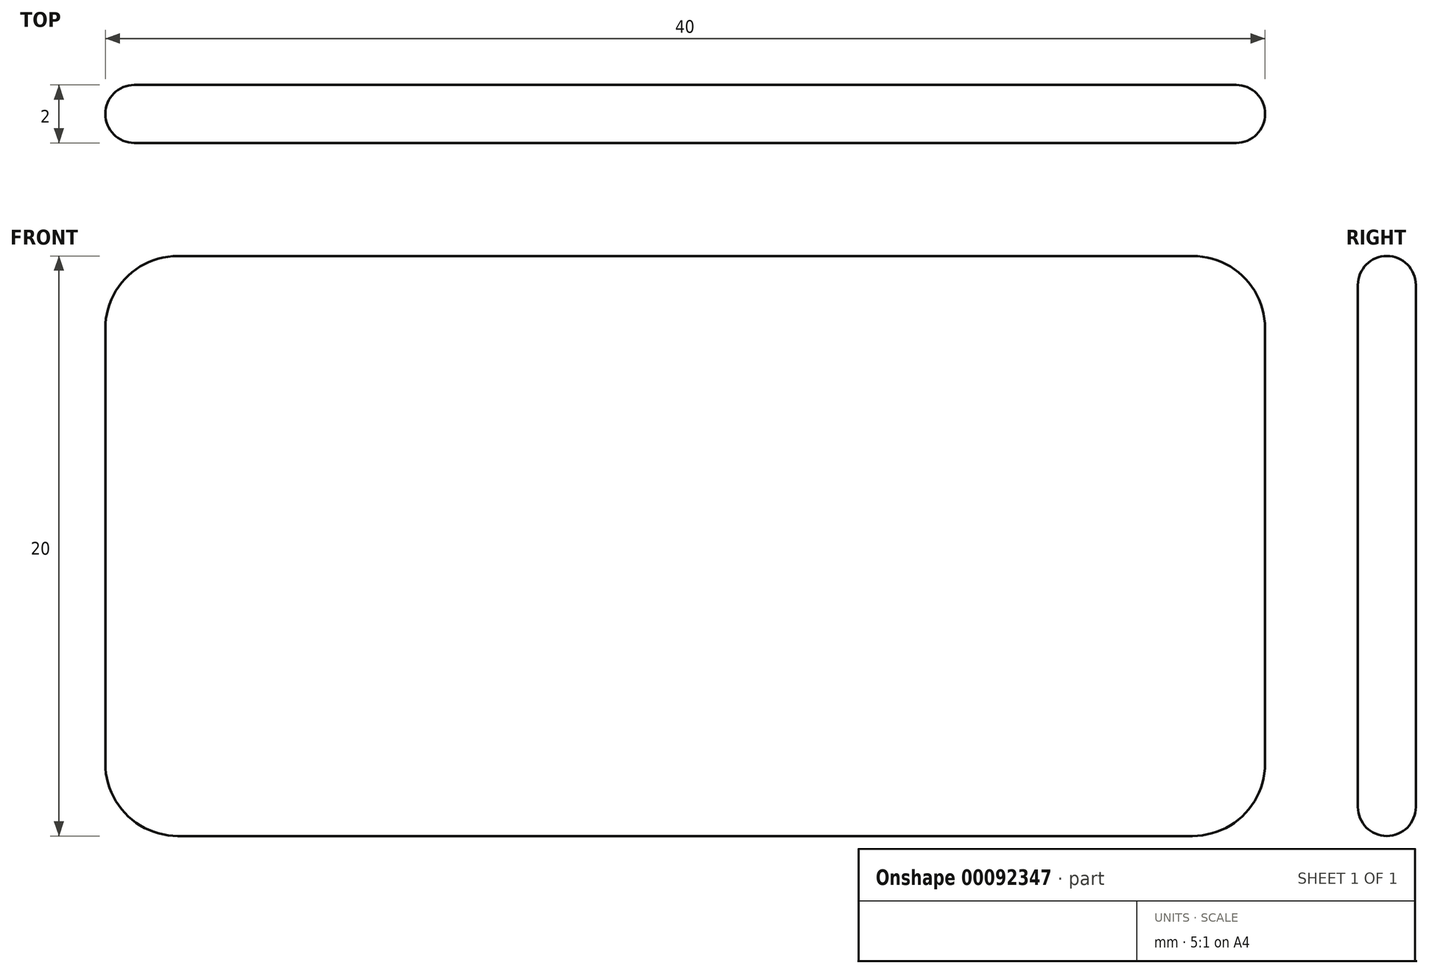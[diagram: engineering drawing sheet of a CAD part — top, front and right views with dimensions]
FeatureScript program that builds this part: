
annotation { "Feature Type Name" : "Feature", "Feature Type Description" : "" }
export const myFeature = defineFeature(function(context is Context, id is Id, definition is map)
    precondition{}
    {
        {
            var Q0;
            Q0=qCreatedBy(makeId("Front.planeOp"),FACE);
            var sketch = newSketch(context, id + "F0", { "sketchPlane" : qUnion([Q0])});
            skLineSegment(sketch, "E0.bottom", {"start": v(2.5, 0) * mm, "end": v(37.5, 0) * mm});
            skLineSegment(sketch, "E0.top", {"start": v(2.5, 20) * mm, "end": v(37.5, 20) * mm});
            skLineSegment(sketch, "E0.left", {"start": v(0, 2.5) * mm, "end": v(0, 17.5) * mm});
            skLineSegment(sketch, "E0.right", {"start": v(40, 2.5) * mm, "end": v(40, 17.5) * mm});
            skPoint(sketch, "E1.visualSharp", {"position": v(0, 20) * mm});
            skArc(sketch, "E1.filletArc", {"start": v(2.5, 20) * mm, "mid": v(0.73, 19.27) * mm, "end": v(0, 17.5) * mm});
            skPoint(sketch, "E2.visualSharp", {"position": v(0, 0) * mm});
            skArc(sketch, "E2.filletArc", {"start": v(0, 2.5) * mm, "mid": v(0.73, 0.73) * mm, "end": v(2.5, 0) * mm});
            skPoint(sketch, "E3.visualSharp", {"position": v(40, 0) * mm});
            skArc(sketch, "E3.filletArc", {"start": v(37.5, 0) * mm, "mid": v(39.27, 0.73) * mm, "end": v(40, 2.5) * mm});
            skPoint(sketch, "E4.visualSharp", {"position": v(40, 20) * mm});
            skArc(sketch, "E4.filletArc", {"start": v(40, 17.5) * mm, "mid": v(39.27, 19.27) * mm, "end": v(37.5, 20) * mm});
            skSolve(sketch);
        }
        {
            var Q0;
            Q0=makeQuery(id+"F0.imprint","IMPRINT",FACE,{"disambiguationData":[TD([[makeQuery(id+"F0.imprint","IMPRINT",EDGE,{"derivedFrom":sQuery(id+"F0.wireOp",EDGE,"E0.bottom")}),1.0]])]});
            extrude(context, id + "F1", {"entities" : qUnion([Q0]), "depth" : 2 * mm});
        }
        {
            var Q0;
            Q0=makeQuery(id+"F1.opExtrude","CAP_EDGE",EDGE,{"disambiguationData":[OSD([sQuery(id+"F0.wireOp",EDGE,"E0.top")])],"isStart":false});
            var Q1;
            Q1=makeQuery(id+"F1.opExtrude","CAP_EDGE",EDGE,{"disambiguationData":[OSD([sQuery(id+"F0.wireOp",EDGE,"E0.top")])],"isStart":true});
            fillet(context, id + "F2", {"entities" : qUnion([Q0, Q1]), "radius" : 1 * mm, "tangentPropagation" : true, "allowEdgeOverflow" : false});
        }
    });
